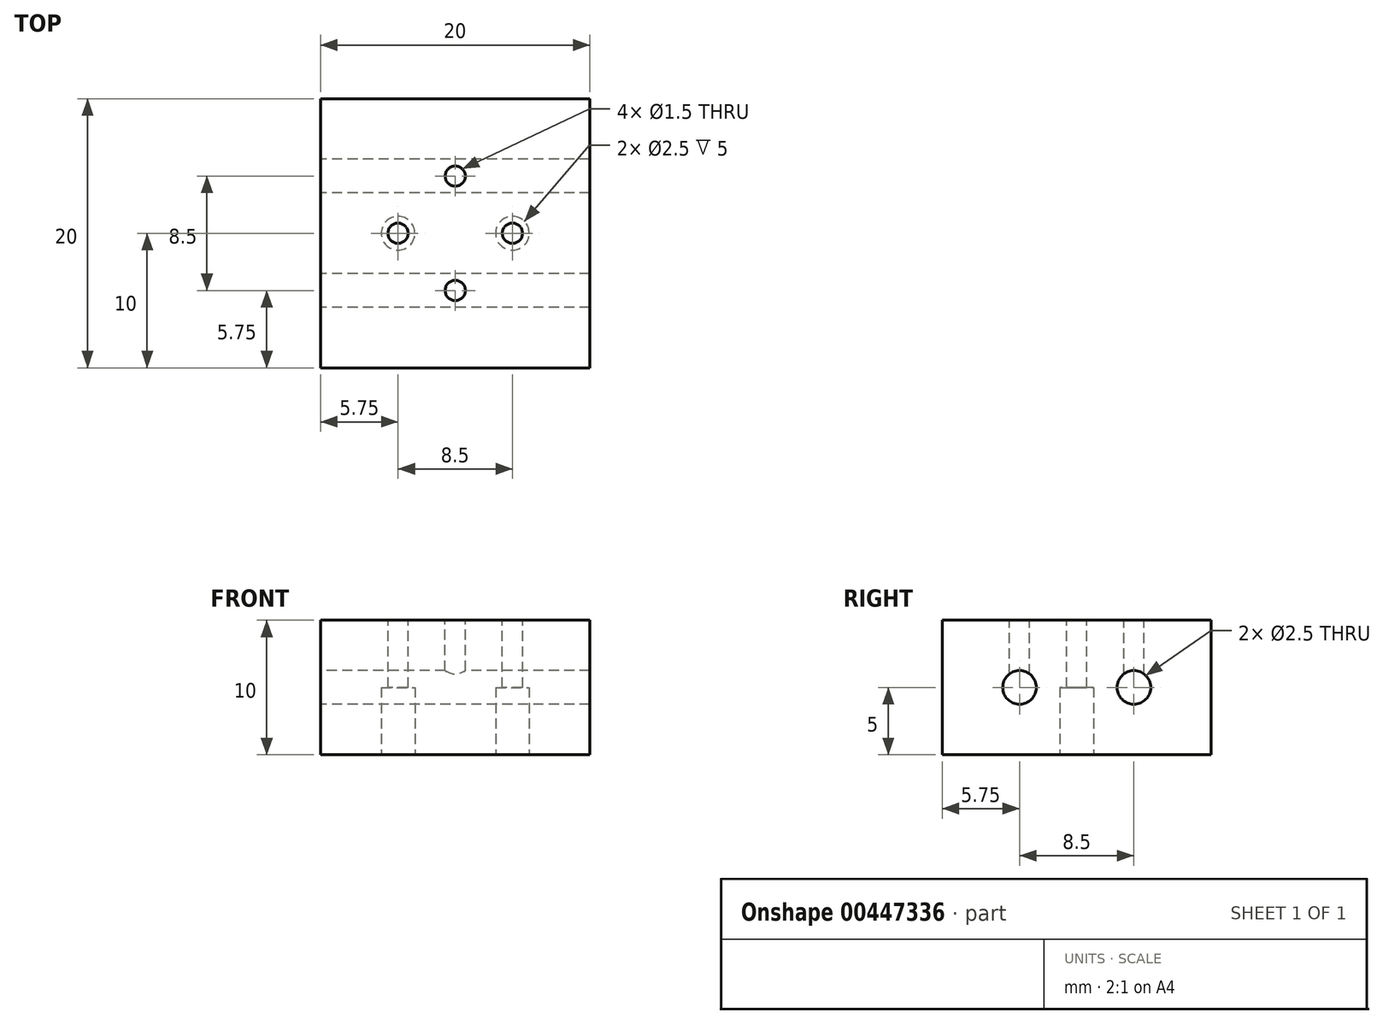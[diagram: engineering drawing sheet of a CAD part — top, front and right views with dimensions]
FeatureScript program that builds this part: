
annotation { "Feature Type Name" : "Feature", "Feature Type Description" : "" }
export const myFeature = defineFeature(function(context is Context, id is Id, definition is map)
    precondition{}
    {
        {
            var Q0;
            Q0=qCreatedBy(makeId("Top.planeOp"),FACE);
            var sketch = newSketch(context, id + "F0", { "sketchPlane" : qUnion([Q0])});
            skLineSegment(sketch, "E0.bottom", {"start": v(0, 0) * mm, "end": v(20, 0) * mm});
            skLineSegment(sketch, "E0.top", {"start": v(0, -20) * mm, "end": v(20, -20) * mm});
            skLineSegment(sketch, "E0.left", {"start": v(0, 0) * mm, "end": v(0, -20) * mm});
            skLineSegment(sketch, "E1", {"start": v(20, 0) * mm, "end": v(20, -20) * mm});
            skLineSegment(sketch, "E2", {"start": v(0, -10) * mm, "end": v(20, -10) * mm, "construction": true});
            skCircle(sketch, "E3", {"center": v(10, -10) * mm, "radius": 6 * mm, "construction": true});
            skCircle(sketch, "E4", {"center": v(10, -10) * mm, "radius": 5 * mm, "construction": true});
            skCircle(sketch, "E5", {"center": v(10, -10) * mm, "radius": 3.5 * mm, "construction": true});
            skCircle(sketch, "E6", {"center": v(10, -10) * mm, "radius": 2 * mm, "construction": true});
            skCircle(sketch, "E7", {"center": v(10, -10) * mm, "radius": 4.25 * mm, "construction": true});
            skCircle(sketch, "E8", {"center": v(10, -14.25) * mm, "radius": 0.75 * mm});
            skCircle(sketch, "E9", {"center": v(5.75, -10) * mm, "radius": 0.75 * mm});
            skCircle(sketch, "E10", {"center": v(10, -5.75) * mm, "radius": 0.75 * mm});
            skCircle(sketch, "E11", {"center": v(14.25, -10) * mm, "radius": 0.75 * mm});
            skCircle(sketch, "E12", {"center": v(10, -10) * mm, "radius": 7 * mm});
            skCircle(sketch, "E13", {"center": v(10, -10) * mm, "radius": 8 * mm});
            skSolve(sketch);
        }
        {
            var Q0;
            Q0=makeQuery(id+"F0.imprint","IMPRINT",FACE,{"disambiguationData":[TD([[makeQuery(id+"F0.imprint","IMPRINT",EDGE,{"derivedFrom":sQuery(id+"F0.wireOp",EDGE,"E0.bottom")}),-1.0]])]});
            var Q1;
            Q1=makeQuery(id+"F0.imprint","IMPRINT",FACE,{"disambiguationData":[TD([[makeQuery(id+"F0.imprint","IMPRINT",EDGE,{"derivedFrom":sQuery(id+"F0.wireOp",EDGE,"E8")}),1.0]])]});
            var Q2;
            Q2=makeQuery(id+"F0.imprint","IMPRINT",FACE,{"disambiguationData":[TD([[makeQuery(id+"F0.imprint","IMPRINT",EDGE,{"derivedFrom":sQuery(id+"F0.wireOp",EDGE,"E10")}),1.0]])]});
            var Q3;
            Q3=makeQuery(id+"F0.imprint","IMPRINT",FACE,{"disambiguationData":[TD([[makeQuery(id+"F0.imprint","IMPRINT",EDGE,{"derivedFrom":sQuery(id+"F0.wireOp",EDGE,"E8")}),-1.0]])]});
            var Q4;
            Q4=makeQuery(id+"F0.imprint","IMPRINT",FACE,{"disambiguationData":[TD([[makeQuery(id+"F0.imprint","IMPRINT",EDGE,{"derivedFrom":sQuery(id+"F0.wireOp",EDGE,"E12")}),-1.0]])]});
            extrude(context, id + "F1", {"entities" : qUnion([Q0, Q1, Q2, Q3, Q4]), "oppositeDirection" : true, "depth" : 10 * mm});
        }
        {
            var Q0;
            Q0=makeQuery(id+"F1.opExtrude","SWEPT_FACE",FACE,{"disambiguationData":[OSD([sQuery(id+"F0.wireOp",EDGE,"E0.left")])]});
            var sketch = newSketch(context, id + "F2", { "sketchPlane" : qUnion([Q0])});
            skCircle(sketch, "E14", {"center": v(5.75, -5) * mm, "radius": 1.25 * mm});
            skCircle(sketch, "E15", {"center": v(14.25, -5) * mm, "radius": 1.25 * mm});
            skLineSegment(sketch, "E16", {"start": v(0, -5) * mm, "end": v(5.75, -5) * mm, "construction": true});
            skLineSegment(sketch, "E17", {"start": v(20, -5) * mm, "end": v(14.25, -5) * mm, "construction": true});
            skSolve(sketch);
        }
        {
            var Q0;
            Q0=makeQuery(id+"F2.imprint","IMPRINT",FACE,{"disambiguationData":[TD([[makeQuery(id+"F2.imprint","IMPRINT",EDGE,{"derivedFrom":sQuery(id+"F2.wireOp",EDGE,"E14")}),1.0]])]});
            var Q1;
            Q1=makeQuery(id+"F2.imprint","IMPRINT",FACE,{"disambiguationData":[TD([[makeQuery(id+"F2.imprint","IMPRINT",EDGE,{"derivedFrom":sQuery(id+"F2.wireOp",EDGE,"E15")}),1.0]])]});
            extrude(context, id + "F3", {"entities" : qUnion([Q0, Q1]), "operationType" : NewBodyOperationType.REMOVE, "oppositeDirection" : true, "depth" : 25 * mm});
        }
        {
            var Q0;
            Q0=makeQuery(id+"F0.imprint","IMPRINT",FACE,{"disambiguationData":[TD([[makeQuery(id+"F0.imprint","IMPRINT",EDGE,{"derivedFrom":sQuery(id+"F0.wireOp",EDGE,"E10")}),1.0]])]});
            var Q1;
            Q1=makeQuery(id+"F0.imprint","IMPRINT",FACE,{"disambiguationData":[TD([[makeQuery(id+"F0.imprint","IMPRINT",EDGE,{"derivedFrom":sQuery(id+"F0.wireOp",EDGE,"E8")}),1.0]])]});
            extrude(context, id + "F4", {"entities" : qUnion([Q0, Q1]), "operationType" : NewBodyOperationType.REMOVE, "oppositeDirection" : true, "depth" : 6 * mm});
        }
        {
            var Q0;
            Q0=makeQuery(id+"F1.opExtrude","CAP_FACE",FACE,{"disambiguationData":[OSD([sQuery(id+"F0.wireOp",EDGE,"E0.bottom"),sQuery(id+"F0.wireOp",EDGE,"E0.top"),sQuery(id+"F0.wireOp",EDGE,"E0.left"),sQuery(id+"F0.wireOp",EDGE,"E1"),sQuery(id+"F0.wireOp",EDGE,"E9"),sQuery(id+"F0.wireOp",EDGE,"E11")])],"isStart":false});
            var sketch = newSketch(context, id + "F5", { "sketchPlane" : qUnion([Q0])});
            skCircle(sketch, "E18", {"center": v(5.75, 10) * mm, "radius": 1.25 * mm});
            skCircle(sketch, "E19", {"center": v(14.25, 10) * mm, "radius": 1.25 * mm});
            skSolve(sketch);
        }
        {
            var Q0;
            Q0=makeQuery(id+"F5.imprint","IMPRINT",FACE,{"disambiguationData":[TD([[makeQuery(id+"F5.imprint","IMPRINT",EDGE,{"derivedFrom":sQuery(id+"F5.wireOp",EDGE,"E18")}),1.0]])]});
            var Q1;
            Q1=makeQuery(id+"F5.imprint","IMPRINT",FACE,{"disambiguationData":[TD([[makeQuery(id+"F5.imprint","IMPRINT",EDGE,{"derivedFrom":sQuery(id+"F5.wireOp",EDGE,"E19")}),1.0]])]});
            extrude(context, id + "F6", {"entities" : qUnion([Q0, Q1]), "operationType" : NewBodyOperationType.REMOVE, "oppositeDirection" : true, "depth" : 5 * mm});
        }
    });
